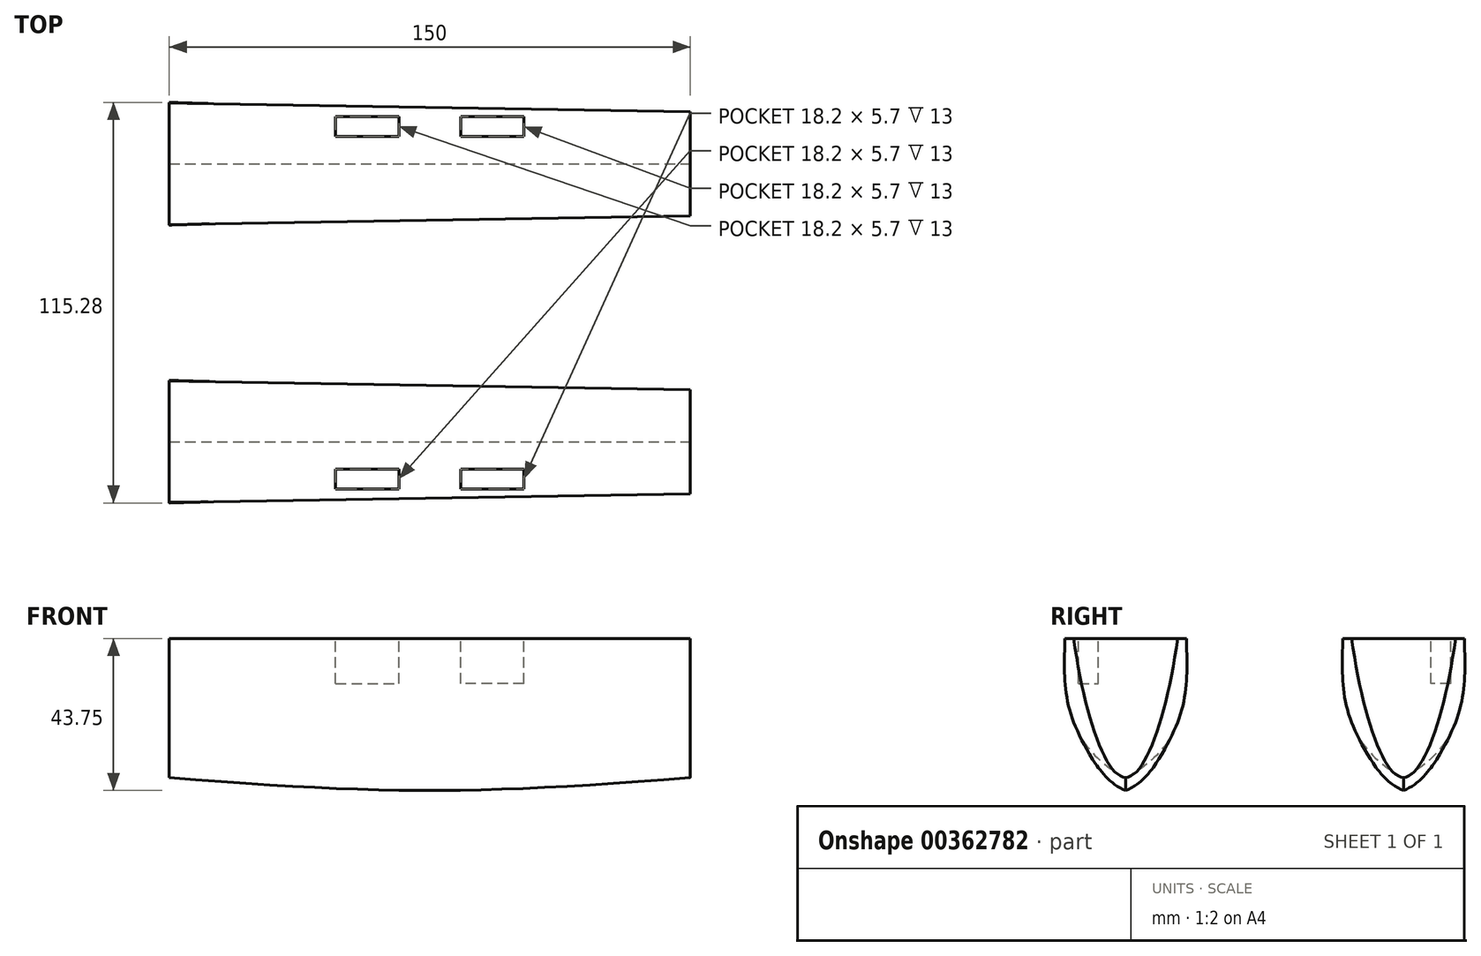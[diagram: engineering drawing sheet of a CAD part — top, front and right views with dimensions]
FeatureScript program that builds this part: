
annotation { "Feature Type Name" : "Feature", "Feature Type Description" : "" }
export const myFeature = defineFeature(function(context is Context, id is Id, definition is map)
    precondition{}
    {
        {
            var Q0;
            Q0=qCreatedBy(makeId("Right.planeOp"),FACE);
            cPlane(context, id + "F0", {"entities" : qUnion([Q0]), "cplaneType" : CPlaneType.OFFSET, "offset" : 150 * mm, "oppositeDirection" : true, "width" : 150 * mm, "height" : 150 * mm});
        }
        {
            var Q0;
            Q0=qCreatedBy(id+"F0.planeOp",FACE);
            var sketch = newSketch(context, id + "F1", { "sketchPlane" : qUnion([Q0])});
            skLineSegment(sketch, "E0", {"start": v(40, 2.15) * mm, "end": v(40, -40) * mm, "construction": true});
            skLineSegment(sketch, "E1", {"start": v(40, 0) * mm, "end": v(22.5, 0) * mm, "construction": true});
            skLineSegment(sketch, "E2", {"start": v(40, 0) * mm, "end": v(22.5, 0) * mm});
            skLineSegment(sketch, "E3.MirrorCS", {"start": v(40, 0) * mm, "end": v(57.5, 0) * mm});
            skFitSpline(sketch, "E4", {"points": [v(22.5, 0) * mm, v(40, -40) * mm], "startDerivative": vector(-0.36, -30) * mm, "endDerivative": vector(60, -30) * mm});
            skFitSpline(sketch, "E5", {"points": [v(57.5, 0) * mm, v(40, -40) * mm], "startDerivative": vector(0.32, -30) * mm, "endDerivative": vector(-60, -30) * mm});
            skFitSpline(sketch, "E6.MirrorCS", {"points": [v(-22.5, 0) * mm, v(-40, -40) * mm], "startDerivative": vector(0.36, -30) * mm, "endDerivative": vector(-60, -30) * mm});
            skFitSpline(sketch, "E7.MirrorCS", {"points": [v(-57.5, 0) * mm, v(-40, -40) * mm], "startDerivative": vector(-0.32, -30) * mm, "endDerivative": vector(60, -30) * mm});
            skLineSegment(sketch, "E8", {"start": v(-22.5, 0) * mm, "end": v(-57.5, 0) * mm});
            skLineSegment(sketch, "E9", {"start": v(-40, -40) * mm, "end": v(-40, 0) * mm, "construction": true});
            skSolve(sketch);
        }
        {
            var Q0;
            Q0=qCreatedBy(makeId("Right.planeOp"),FACE);
            var sketch = newSketch(context, id + "F2", { "sketchPlane" : qUnion([Q0])});
            skFitSpline(sketch, "E10", {"points": [v(-55, 0) * mm, v(-40, -40) * mm, v(-25, 0) * mm], "startDerivative": vector(18, -126) * mm, "endDerivative": vector(18, 126) * mm});
            skLineSegment(sketch, "E11", {"start": v(-40, -40) * mm, "end": v(-40, 0) * mm, "construction": true});
            skFitSpline(sketch, "E12.MirrorCS", {"points": [v(55, 0) * mm, v(40, -40) * mm, v(25, 0) * mm], "startDerivative": vector(-18, -126) * mm, "endDerivative": vector(-18, 126) * mm});
            skLineSegment(sketch, "E13", {"start": v(25, 0) * mm, "end": v(55, 0) * mm});
            skLineSegment(sketch, "E14", {"start": v(-40, 0) * mm, "end": v(-25, 0) * mm});
            skLineSegment(sketch, "E15", {"start": v(40, -40) * mm, "end": v(40, 0) * mm, "construction": true});
            skLineSegment(sketch, "E16", {"start": v(-25, 0) * mm, "end": v(-55, 0) * mm});
            skSolve(sketch);
        }
        {
            var Q0;
            Q0=qCreatedBy(makeId("Top.planeOp"),FACE);
            var sketch = newSketch(context, id + "F3", { "sketchPlane" : qUnion([Q0])});
            skFitSpline(sketch, "E17", {"points": [v(-150, -22.5) * mm, v(0, -25) * mm], "startDerivative": vector(195, 4.5) * mm, "endDerivative": vector(195, -15) * mm});
            skFitSpline(sketch, "E18", {"points": [v(-150, 57.5) * mm, v(0, 55) * mm], "startDerivative": vector(195, 4.5) * mm, "endDerivative": vector(195, -15) * mm});
            skFitSpline(sketch, "E19.MirrorCS", {"points": [v(-150, 22.5) * mm, v(0, 25) * mm], "startDerivative": vector(195, -4.5) * mm, "endDerivative": vector(195, 15) * mm});
            skFitSpline(sketch, "E20.MirrorCS", {"points": [v(-150, -57.5) * mm, v(0, -55) * mm], "startDerivative": vector(195, -4.5) * mm, "endDerivative": vector(195, 15) * mm});
            skSolve(sketch);
        }
        {
            var Q0;
            Q0=qCreatedBy(makeId("Front.planeOp"),FACE);
            cPlane(context, id + "F4", {"entities" : qUnion([Q0]), "cplaneType" : CPlaneType.OFFSET, "offset" : 40 * mm, "width" : 150 * mm, "height" : 150 * mm});
        }
        {
            var Q0;
            Q0=qCreatedBy(id+"F4.planeOp",FACE);
            var sketch = newSketch(context, id + "F5", { "sketchPlane" : qUnion([Q0])});
            skFitSpline(sketch, "E21", {"points": [v(-150, -40) * mm, v(0, -40) * mm], "startDerivative": vector(180, -15) * mm, "endDerivative": vector(180, 15) * mm});
            skSolve(sketch);
        }
        {
            var Q0;
            Q0=qCreatedBy(makeId("Front.planeOp"),FACE);
            cPlane(context, id + "F6", {"entities" : qUnion([Q0]), "cplaneType" : CPlaneType.OFFSET, "offset" : 40 * mm, "oppositeDirection" : true, "width" : 150 * mm, "height" : 150 * mm});
        }
        {
            var Q0;
            Q0=makeQuery(id+"F1.imprint","IMPRINT",FACE,{"disambiguationData":[TD([[makeQuery(id+"F1.imprint","IMPRINT",EDGE,{"derivedFrom":sQuery(id+"F1.wireOp",EDGE,"E6.MirrorCS")}),-1.0]])]});
            var Q1;
            {var subQ0=sQuery(id+"F2.wireOp",EDGE,"E10");Q1=makeQuery(id+"F2.imprint","IMPRINT",FACE,{"disambiguationData":[TD([[makeQuery(id+"F2.imprint","IMPRINT",EDGE,{"derivedFrom":subQ0}),1.0]])]});}
            var Q2;
            Q2=qConstructionFilter(qBodyType(qCreatedBy(id+"F5",EDGE),BodyType.WIRE),ConstructionObject.NO);
            loft(context, id + "F7", {"addGuides" : true, "sheetProfilesArray" : [{ "sheetProfileEntities" : qUnion([Q0]) }, { "sheetProfileEntities" : qUnion([Q1]) }], "guidesArray" : [{ "guideEntities" : qUnion([Q2]), "guideDerivativeType" : LoftGuideDerivativeType.DEFAULT, "guideDerivativeMagnitude" : 1 }]});
        }
        {
            var Q0;
            Q0=makeQuery(id+"F7.opLoft","SWEPT_BODY",BODY,{"disambiguationData":[OSD([makeQuery(id+"F1.imprint","IMPRINT",FACE,{"disambiguationData":[TD([[makeQuery(id+"F1.imprint","IMPRINT",EDGE,{"derivedFrom":sQuery(id+"F1.wireOp",EDGE,"E6.MirrorCS")}),-1.0]])]}),makeQuery(id+"F2.imprint","IMPRINT",FACE,{"disambiguationData":[TD([[makeQuery(id+"F2.imprint","IMPRINT",EDGE,{"derivedFrom":sQuery(id+"F2.wireOp",EDGE,"E10")}),1.0]])]}),sQuery(id+"F3.wireOp",EDGE,"E17"),sQuery(id+"F3.wireOp",EDGE,"ee1c5fa2-1868-4677-8e25-8bf4c0bb29820.MirrorCS"),sQuery(id+"F5.wireOp",EDGE,"E21")])]});
            var Q1;
            Q1=qCreatedBy(makeId("Front.planeOp"),FACE);
            mirror(context, id + "F8", {"entities" : qUnion([Q0]), "mirrorPlane" : qUnion([Q1])});
        }
        {
            var Q0;
            Q0=makeQuery(id+"F8.opPattern","COPY",FACE,{"derivedFrom":makeQuery(id+"F7.opLoft","SWEPT_FACE",FACE,{"disambiguationData":[OSD([sQuery(id+"F1.wireOp",EDGE,"E6.MirrorCS"),sQuery(id+"F1.wireOp",EDGE,"E7.MirrorCS"),sQuery(id+"F1.wireOp",EDGE,"E8"),sQuery(id+"F2.wireOp",EDGE,"E10"),sQuery(id+"F2.wireOp",EDGE,"E16")])]}),"instanceName":"1"});
            var sketch = newSketch(context, id + "F9", { "sketchPlane" : qUnion([Q0])});
            skLineSegment(sketch, "E22", {"start": v(-75, 56.25) * mm, "end": v(-75, -78.33) * mm, "construction": true});
            skLineSegment(sketch, "E23.bottom", {"start": v(-45, -57.5) * mm, "end": v(-105, -57.5) * mm, "construction": true});
            skLineSegment(sketch, "E23.top", {"start": v(-45, 57.5) * mm, "end": v(-105, 57.5) * mm, "construction": true});
            skLineSegment(sketch, "E23.left", {"start": v(-45, -57.5) * mm, "end": v(-45, 57.5) * mm, "construction": true});
            skLineSegment(sketch, "E23.right", {"start": v(-105, -57.5) * mm, "end": v(-105, 57.5) * mm, "construction": true});
            skPoint(sketch, "E23.middle", {"position": v(-75, 0) * mm});
            skLineSegment(sketch, "E24.bottom", {"start": v(-102.1, 53.6) * mm, "end": v(-83.9, 53.6) * mm});
            skLineSegment(sketch, "E24.top", {"start": v(-102.1, 47.9) * mm, "end": v(-83.9, 47.9) * mm});
            skLineSegment(sketch, "E24.left", {"start": v(-102.1, 53.6) * mm, "end": v(-102.1, 47.9) * mm});
            skLineSegment(sketch, "E24.right", {"start": v(-83.9, 53.6) * mm, "end": v(-83.9, 47.9) * mm});
            skLineSegment(sketch, "E25.MirrorCS", {"start": v(-47.9, 47.9) * mm, "end": v(-66.1, 47.9) * mm});
            skLineSegment(sketch, "E26.MirrorCS", {"start": v(-47.9, 53.6) * mm, "end": v(-66.1, 53.6) * mm});
            skLineSegment(sketch, "E27.MirrorCS", {"start": v(-47.9, 53.6) * mm, "end": v(-47.9, 47.9) * mm});
            skLineSegment(sketch, "E28.MirrorCS", {"start": v(-66.1, 53.6) * mm, "end": v(-66.1, 47.9) * mm});
            skLineSegment(sketch, "E29", {"start": v(-105, 0) * mm, "end": v(0, 0) * mm, "construction": true});
            skLineSegment(sketch, "E30.MirrorCS", {"start": v(-102.1, -47.9) * mm, "end": v(-83.9, -47.9) * mm});
            skLineSegment(sketch, "E31.MirrorCS", {"start": v(-102.1, -53.6) * mm, "end": v(-102.1, -47.9) * mm});
            skLineSegment(sketch, "E32.MirrorCS", {"start": v(-102.1, -53.6) * mm, "end": v(-83.9, -53.6) * mm});
            skLineSegment(sketch, "E33.MirrorCS", {"start": v(-83.9, -53.6) * mm, "end": v(-83.9, -47.9) * mm});
            skLineSegment(sketch, "E34.MirrorCS", {"start": v(-47.9, -47.9) * mm, "end": v(-66.1, -47.9) * mm});
            skLineSegment(sketch, "E35.MirrorCS", {"start": v(-47.9, -53.6) * mm, "end": v(-66.1, -53.6) * mm});
            skLineSegment(sketch, "E36.MirrorCS", {"start": v(-66.1, -53.6) * mm, "end": v(-66.1, -47.9) * mm});
            skLineSegment(sketch, "E37.MirrorCS", {"start": v(-47.9, -53.6) * mm, "end": v(-47.9, -47.9) * mm});
            skSolve(sketch);
        }
        {
            var Q0;
            Q0=qSketchRegion(id+"F9",true);
            extrude(context, id + "F10", {"entities" : qUnion([Q0]), "operationType" : NewBodyOperationType.REMOVE, "oppositeDirection" : true, "depth" : 13 * mm});
        }
    });
